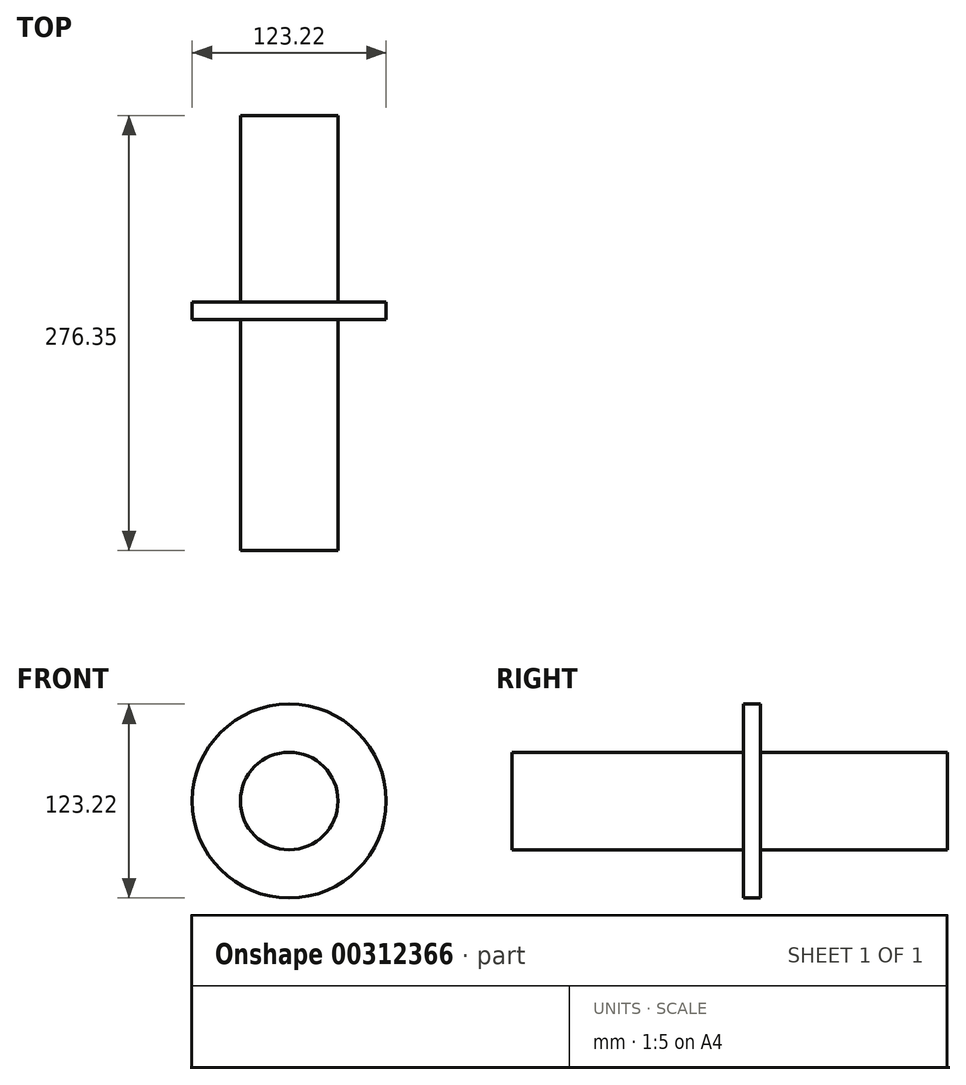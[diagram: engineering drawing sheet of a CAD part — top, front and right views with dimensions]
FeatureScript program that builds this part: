
annotation { "Feature Type Name" : "Feature", "Feature Type Description" : "" }
export const myFeature = defineFeature(function(context is Context, id is Id, definition is map)
    precondition{}
    {
        {
            var Q0;
            Q0=qCreatedBy(makeId("Front.planeOp"),FACE);
            var sketch = newSketch(context, id + "F0", { "sketchPlane" : qUnion([Q0])});
            skCircle(sketch, "E0", {"center": v(0, 0) * mm, "radius": 61.6 * mm});
            skCircle(sketch, "E1", {"center": v(0, 0) * mm, "radius": 31 * mm});
            skSolve(sketch);
        }
        {
            var Q0;
            Q0=makeQuery(id+"F0.imprint","IMPRINT",FACE,{"disambiguationData":[TD([[makeQuery(id+"F0.imprint","IMPRINT",EDGE,{"derivedFrom":sQuery(id+"F0.wireOp",EDGE,"E1")}),1.0]])]});
            extrude(context, id + "F1", {"entities" : qUnion([Q0]), "depth" : 157.73 * mm, "hasSecondDirection" : true, "secondDirectionOppositeDirection" : true, "secondDirectionDepth" : 118.62 * mm});
        }
        {
            var Q0;
            Q0=makeQuery(id+"F0.imprint","IMPRINT",FACE,{"disambiguationData":[TD([[makeQuery(id+"F0.imprint","IMPRINT",EDGE,{"derivedFrom":sQuery(id+"F0.wireOp",EDGE,"E0")}),1.0]])]});
            extrude(context, id + "F2", {"entities" : qUnion([Q0]), "operationType" : NewBodyOperationType.ADD, "depth" : 10.92 * mm});
        }
    });
